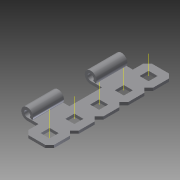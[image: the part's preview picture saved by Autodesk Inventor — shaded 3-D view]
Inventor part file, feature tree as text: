
AUTODESK INVENTOR PART (.ipt)
format: ipt  version: 2015 (Build 190159000, 159)  size: 159,744 bytes
history: native  units: in
note: dims shown in document units (in); Inventor stores cm internally (conversion verified against a paired STEP export)
features: other x8, pattern_linear x1, imported_body x1
ambient origin geometry x8: Origin, YZ Plane, XZ Plane, XY Plane, X Axis, Y Axis, Z Axis, Center Point
bodies: Body1 (feature_tree)
feature tree (10):
  other  "Cut-Extrude3"
  other  "Hinge Plate"
  other  "axis"
  pattern_linear  "axes"  Count1=5 Spacing1=0.5in
  imported_body  "Base1"
  other  "Work Point1"
  other  "Work Axis2"
  other  "Work Axis3"
  other  "Work Axis4"
  other  "Work Axis5"
